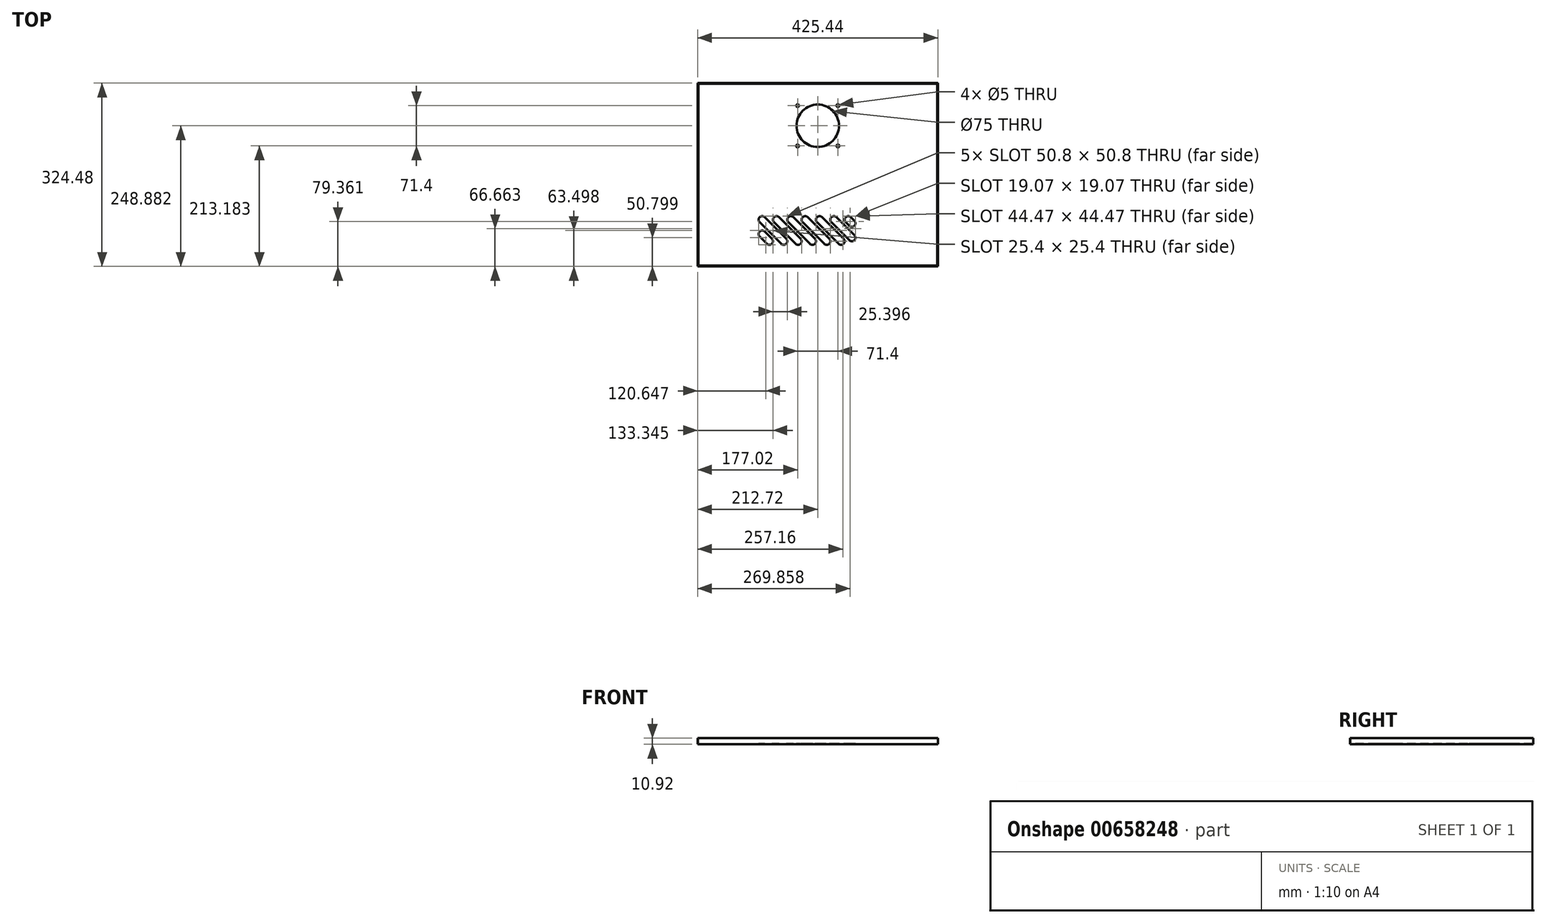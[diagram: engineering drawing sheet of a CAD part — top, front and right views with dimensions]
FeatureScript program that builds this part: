
annotation { "Feature Type Name" : "Feature", "Feature Type Description" : "" }
export const myFeature = defineFeature(function(context is Context, id is Id, definition is map)
    precondition{}
    {
        {
            var Q0;
            Q0=qCreatedBy(makeId("Top.planeOp"),FACE);
            var sketch = newSketch(context, id + "F0", { "sketchPlane" : qUnion([Q0])});
            skLineSegment(sketch, "E0.bottom", {"start": v(-212.73, 162.24) * mm, "end": v(212.73, 162.24) * mm});
            skLineSegment(sketch, "E0.top", {"start": v(-212.73, -162.24) * mm, "end": v(212.72, -162.24) * mm});
            skLineSegment(sketch, "E0.left", {"start": v(-212.72, 162.24) * mm, "end": v(-212.72, -162.24) * mm});
            skLineSegment(sketch, "E0.right", {"start": v(212.73, 162.24) * mm, "end": v(212.73, -162.24) * mm});
            skPoint(sketch, "E1", {"position": v(0, 162.24) * mm});
            skPoint(sketch, "E2", {"position": v(-212.73, 0) * mm});
            skLineSegment(sketch, "E3", {"start": v(-212.72, 124.14) * mm, "end": v(212.72, 124.14) * mm, "construction": true});
            skCircle(sketch, "E4", {"center": v(0, 86.64) * mm, "radius": 37.5 * mm});
            skPoint(sketch, "E4.centerSnap0", {"position": v(0, 124.14) * mm});
            skLineSegment(sketch, "E5", {"start": v(0, 86.64) * mm, "end": v(-35.7, 86.64) * mm, "construction": true});
            skPoint(sketch, "E6", {"position": v(-35.7, 86.64) * mm});
            skLineSegment(sketch, "E7.bottom", {"start": v(-35.7, 122.34) * mm, "end": v(35.7, 122.34) * mm, "construction": true});
            skLineSegment(sketch, "E7.top", {"start": v(-35.7, 50.94) * mm, "end": v(35.7, 50.94) * mm, "construction": true});
            skLineSegment(sketch, "E7.left", {"start": v(-35.7, 122.34) * mm, "end": v(-35.7, 50.94) * mm, "construction": true});
            skLineSegment(sketch, "E7.right", {"start": v(35.7, 122.34) * mm, "end": v(35.7, 50.94) * mm, "construction": true});
            skCircle(sketch, "E8", {"center": v(-35.7, 122.34) * mm, "radius": 2.5 * mm});
            skCircle(sketch, "E9", {"center": v(35.7, 122.34) * mm, "radius": 2.5 * mm});
            skCircle(sketch, "E10", {"center": v(35.7, 50.94) * mm, "radius": 2.5 * mm});
            skCircle(sketch, "E11", {"center": v(-35.7, 50.94) * mm, "radius": 2.5 * mm});
            skLineSegment(sketch, "E12", {"start": v(-212.73, -124.14) * mm, "end": v(212.73, -124.14) * mm, "construction": true});
            skLineSegment(sketch, "E13.bottom", {"start": v(-104.78, -124.14) * mm, "end": v(66.67, -124.14) * mm, "construction": true});
            skLineSegment(sketch, "E13.top", {"start": v(-104.78, -73.34) * mm, "end": v(66.67, -73.34) * mm, "construction": true});
            skLineSegment(sketch, "E13.left", {"start": v(-104.78, -124.14) * mm, "end": v(-104.78, -73.34) * mm, "construction": true});
            skLineSegment(sketch, "E13.right", {"start": v(66.67, -124.14) * mm, "end": v(66.67, -108.83) * mm, "construction": true});
            skLineSegment(sketch, "E14", {"start": v(-104.78, -73.34) * mm, "end": v(-53.98, -124.14) * mm, "construction": true});
            skLineSegment(sketch, "E15", {"start": v(-79.38, -73.34) * mm, "end": v(-28.58, -124.14) * mm, "construction": true});
            skLineSegment(sketch, "E16", {"start": v(-104.78, -98.74) * mm, "end": v(-79.37, -124.14) * mm, "construction": true});
            skLineSegment(sketch, "E17", {"start": v(-53.98, -73.34) * mm, "end": v(-3.18, -124.14) * mm, "construction": true});
            skLineSegment(sketch, "E18", {"start": v(-28.59, -73.34) * mm, "end": v(22.21, -124.14) * mm, "construction": true});
            skLineSegment(sketch, "E19", {"start": v(-3.2, -73.34) * mm, "end": v(47.6, -124.14) * mm, "construction": true});
            skLineSegment(sketch, "E20", {"start": v(22.2, -73.34) * mm, "end": v(66.67, -117.81) * mm, "construction": true});
            skLineSegment(sketch, "E21", {"start": v(47.6, -73.34) * mm, "end": v(66.67, -92.42) * mm, "construction": true});
            skLineSegment(sketch, "E22", {"start": v(-93.93, -75.2) * mm, "end": v(-55.83, -113.3) * mm});
            skLineSegment(sketch, "E23", {"start": v(-102.92, -84.18) * mm, "end": v(-64.82, -122.28) * mm});
            skLineSegment(sketch, "E24", {"start": v(-93.93, -100.6) * mm, "end": v(-81.23, -113.3) * mm});
            skLineSegment(sketch, "E25", {"start": v(-102.92, -109.58) * mm, "end": v(-90.21, -122.28) * mm});
            skArc(sketch, "E26", {"start": v(-93.93, -75.2) * mm, "mid": v(-102.92, -75.2) * mm, "end": v(-102.92, -84.18) * mm});
            skArc(sketch, "E27", {"start": v(-64.82, -122.28) * mm, "mid": v(-55.83, -122.28) * mm, "end": v(-55.83, -113.3) * mm});
            skArc(sketch, "E28", {"start": v(-93.93, -100.6) * mm, "mid": v(-102.92, -100.6) * mm, "end": v(-102.92, -109.58) * mm});
            skArc(sketch, "E29", {"start": v(-90.21, -122.28) * mm, "mid": v(-81.23, -122.28) * mm, "end": v(-81.23, -113.3) * mm});
            skLineSegment(sketch, "E30", {"start": v(-77.52, -84.18) * mm, "end": v(-39.42, -122.28) * mm});
            skLineSegment(sketch, "E31", {"start": v(-68.54, -75.2) * mm, "end": v(-30.44, -113.3) * mm});
            skLineSegment(sketch, "E32", {"start": v(-52.12, -84.18) * mm, "end": v(-14.02, -122.28) * mm});
            skLineSegment(sketch, "E33", {"start": v(-43.14, -75.2) * mm, "end": v(-5.04, -113.3) * mm});
            skLineSegment(sketch, "E34", {"start": v(-26.73, -84.18) * mm, "end": v(11.37, -122.28) * mm});
            skLineSegment(sketch, "E35", {"start": v(-17.75, -75.2) * mm, "end": v(20.35, -113.3) * mm});
            skLineSegment(sketch, "E36", {"start": v(-1.33, -84.18) * mm, "end": v(36.77, -122.28) * mm});
            skLineSegment(sketch, "E37", {"start": v(7.65, -75.2) * mm, "end": v(45.75, -113.3) * mm});
            skLineSegment(sketch, "E38", {"start": v(24.07, -84.18) * mm, "end": v(55.83, -115.95) * mm});
            skLineSegment(sketch, "E39", {"start": v(33.05, -75.2) * mm, "end": v(64.82, -106.97) * mm});
            skLineSegment(sketch, "E40", {"start": v(49.46, -84.18) * mm, "end": v(55.83, -90.56) * mm});
            skLineSegment(sketch, "E41", {"start": v(64.82, -81.58) * mm, "end": v(58.44, -75.2) * mm});
            skArc(sketch, "E42", {"start": v(-68.54, -75.2) * mm, "mid": v(-77.52, -75.2) * mm, "end": v(-77.52, -84.18) * mm});
            skArc(sketch, "E43", {"start": v(-39.42, -122.28) * mm, "mid": v(-30.44, -122.28) * mm, "end": v(-30.44, -113.3) * mm});
            skArc(sketch, "E44", {"start": v(-43.14, -75.2) * mm, "mid": v(-52.12, -75.2) * mm, "end": v(-52.12, -84.18) * mm});
            skArc(sketch, "E45", {"start": v(-14.02, -122.28) * mm, "mid": v(-5.04, -122.28) * mm, "end": v(-5.04, -113.3) * mm});
            skArc(sketch, "E46", {"start": v(-17.75, -75.2) * mm, "mid": v(-26.73, -75.2) * mm, "end": v(-26.73, -84.18) * mm});
            skArc(sketch, "E47", {"start": v(11.37, -122.28) * mm, "mid": v(20.35, -122.28) * mm, "end": v(20.35, -113.3) * mm});
            skArc(sketch, "E48", {"start": v(7.65, -75.2) * mm, "mid": v(-1.33, -75.2) * mm, "end": v(-1.33, -84.18) * mm});
            skArc(sketch, "E49", {"start": v(36.77, -122.28) * mm, "mid": v(45.75, -122.28) * mm, "end": v(45.75, -113.3) * mm});
            skArc(sketch, "E50", {"start": v(33.05, -75.2) * mm, "mid": v(24.07, -75.2) * mm, "end": v(24.07, -84.18) * mm});
            skArc(sketch, "E51", {"start": v(55.83, -115.95) * mm, "mid": v(64.82, -115.95) * mm, "end": v(64.82, -106.97) * mm});
            skArc(sketch, "E52", {"start": v(58.44, -75.2) * mm, "mid": v(49.46, -75.2) * mm, "end": v(49.46, -84.18) * mm});
            skArc(sketch, "E53", {"start": v(55.83, -90.56) * mm, "mid": v(64.82, -90.56) * mm, "end": v(64.82, -81.58) * mm});
            skPoint(sketch, "E54.trimOffspring.end.orphan", {"position": v(66.67, -126.8) * mm});
            skLineSegment(sketch, "E55.trimOffspring", {"start": v(66.67, -92.42) * mm, "end": v(66.67, -73.34) * mm, "construction": true});
            skSolve(sketch);
        }
        {
            var Q0;
            Q0 = qSketchRegion(id + "F0", true);
            extrude(context, id + "F1", {"entities" : qUnion([Q0]), "depth" : 1.27 * mm, "offsetDistance" : 25.4 * mm});
        }
        {
            var Q0;
            Q0=makeQuery(id+"F1.opExtrude","CAP_FACE",FACE,{"disambiguationData":[OSD([sQuery(id+"F0.wireOp",EDGE,"E0.bottom"),sQuery(id+"F0.wireOp",EDGE,"E0.top"),sQuery(id+"F0.wireOp",EDGE,"E0.left"),sQuery(id+"F0.wireOp",EDGE,"E0.right"),sQuery(id+"F0.wireOp",EDGE,"7jo6IiGQ-0Pxl-dtSB-hP8V-GohwB0lIv8zy"),sQuery(id+"F0.wireOp",EDGE,"CWcus5W1-TvBw-SdVc-z0fx-8RuhOfK6xc8F"),sQuery(id+"F0.wireOp",EDGE,"25WvDBuJ-WDR8-f1oW-Pv1g-ajS1InQtg4Az"),sQuery(id+"F0.wireOp",EDGE,"4ANNKCIl-s2rD-lwlz-nPYs-lpA9eLvwclIi"),sQuery(id+"F0.wireOp",EDGE,"4sH5vblm-HvzM-J42n-t4H5-A0vnyWCk8Q3J.top"),sQuery(id+"F0.wireOp",EDGE,"4sH5vblm-HvzM-J42n-t4H5-A0vnyWCk8Q3J.left"),sQuery(id+"F0.wireOp",EDGE,"4sH5vblm-HvzM-J42n-t4H5-A0vnyWCk8Q3J.right"),sQuery(id+"F0.wireOp",EDGE,"yPQRZlpt-DJka-dtDD-WRz3-y5N46tBygwNu.top"),sQuery(id+"F0.wireOp",EDGE,"yPQRZlpt-DJka-dtDD-WRz3-y5N46tBygwNu.left"),sQuery(id+"F0.wireOp",EDGE,"yPQRZlpt-DJka-dtDD-WRz3-y5N46tBygwNu.right"),sQuery(id+"F0.wireOp",EDGE,"h8xEIhus-6Od8-7BV4-SaLn-SGZ2kFKH4c4x"),sQuery(id+"F0.wireOp",EDGE,"DpdJQOZM-D5hJ-pkrL-OmNT-U8qtAstGew7e"),sQuery(id+"F0.wireOp",EDGE,"0QN0Tp38-Cb57-oAa1-AYwf-decZYHKdVhJB.bottom"),sQuery(id+"F0.wireOp",EDGE,"0QN0Tp38-Cb57-oAa1-AYwf-decZYHKdVhJB.top"),sQuery(id+"F0.wireOp",EDGE,"BmFZOFqL-VJhZ-3cVE-qPyU-yJvUDIm0dNII"),sQuery(id+"F0.wireOp",EDGE,"pvhWlNlq-87aa-C4EB-6qQu-4UWn9xWmH4xx"),sQuery(id+"F0.wireOp",EDGE,"32fa5892-eeb3-4547-bd1c-0652c1aa3433.filletArc"),sQuery(id+"F0.wireOp",EDGE,"196a1e8f-6835-4408-8d4e-5a0d6aba8096.filletArc"),sQuery(id+"F0.wireOp",EDGE,"417ab39d-321f-465a-ac69-16b00fd554bb.filletArc"),sQuery(id+"F0.wireOp",EDGE,"0ac3de2a-2022-44de-b6c3-f40354936dca.filletArc"),sQuery(id+"F0.wireOp",EDGE,"yMGYSPlu-KOc6-Z8W9-XLDP-NKw8DFld2Ph4"),sQuery(id+"F0.wireOp",EDGE,"JVqKSmGn-gUrH-NAbh-rB2h-PRdXodRwmpko"),sQuery(id+"F0.wireOp",EDGE,"rhsN3fJI-gD4t-TyU6-Ilzu-4F7E1usGAzwK.top"),sQuery(id+"F0.wireOp",EDGE,"rhsN3fJI-gD4t-TyU6-Ilzu-4F7E1usGAzwK.left"),sQuery(id+"F0.wireOp",EDGE,"rhsN3fJI-gD4t-TyU6-Ilzu-4F7E1usGAzwK.right"),sQuery(id+"F0.wireOp",EDGE,"429SWzlN-nJrN-UhhZ-IVbA-hIjpxZMVZi0I.top"),sQuery(id+"F0.wireOp",EDGE,"429SWzlN-nJrN-UhhZ-IVbA-hIjpxZMVZi0I.left"),sQuery(id+"F0.wireOp",EDGE,"429SWzlN-nJrN-UhhZ-IVbA-hIjpxZMVZi0I.right"),sQuery(id+"F0.wireOp",EDGE,"dmg43G8f-O9ra-vEwY-zvnv-K2DaT5RGJ8GX.bottom"),sQuery(id+"F0.wireOp",EDGE,"dmg43G8f-O9ra-vEwY-zvnv-K2DaT5RGJ8GX.top"),sQuery(id+"F0.wireOp",EDGE,"dmg43G8f-O9ra-vEwY-zvnv-K2DaT5RGJ8GX.left"),sQuery(id+"F0.wireOp",EDGE,"dmg43G8f-O9ra-vEwY-zvnv-K2DaT5RGJ8GX.right"),sQuery(id+"F0.wireOp",EDGE,"kEmnefvy-9gh5-09fB-0LNn-i8JtkV0QkEEa"),sQuery(id+"F0.wireOp",EDGE,"r0IOJuvS-tt7Q-ikGY-QNl2-SYZ859AdofSU"),sQuery(id+"F0.wireOp",EDGE,"5da69efe-eb80-430e-8db8-3bde243bf552.filletArc"),sQuery(id+"F0.wireOp",EDGE,"8770b30c-255e-4eb1-997c-e931af85a35f.filletArc"),sQuery(id+"F0.wireOp",EDGE,"d83a60c7-2247-4e0b-8f29-1b7a022d62f3.filletArc"),sQuery(id+"F0.wireOp",EDGE,"f0b65f8c-8d23-4360-9aaa-58dcffd63d6c.filletArc")])],"isStart":false});
            var sketch = newSketch(context, id + "F2", { "sketchPlane" : qUnion([Q0])});
            skLineSegment(sketch, "E56.bottom", {"start": v(-211.46, 160.97) * mm, "end": v(211.46, 160.97) * mm});
            skLineSegment(sketch, "E56.top", {"start": v(-211.46, -160.97) * mm, "end": v(211.46, -160.97) * mm});
            skLineSegment(sketch, "E56.left", {"start": v(-211.46, 160.97) * mm, "end": v(-211.46, -160.97) * mm});
            skLineSegment(sketch, "E56.right", {"start": v(211.46, 160.97) * mm, "end": v(211.46, -160.97) * mm});
            skLineSegment(sketch, "E57.bottom", {"start": v(-212.73, 162.24) * mm, "end": v(212.73, 162.24) * mm});
            skLineSegment(sketch, "E57.top", {"start": v(-212.73, -162.24) * mm, "end": v(212.73, -162.24) * mm});
            skLineSegment(sketch, "E57.left", {"start": v(-212.73, 162.24) * mm, "end": v(-212.73, -162.24) * mm});
            skLineSegment(sketch, "E57.right", {"start": v(212.73, 162.24) * mm, "end": v(212.73, -162.24) * mm});
            skSolve(sketch);
        }
        {
            var Q0;
            Q0 = qSketchRegion(id + "F2", true);
            extrude(context, id + "F3", {"entities" : qUnion([Q0]), "operationType" : NewBodyOperationType.ADD, "depth" : 9.65 * mm, "offsetDistance" : 25.4 * mm});
        }
    });
